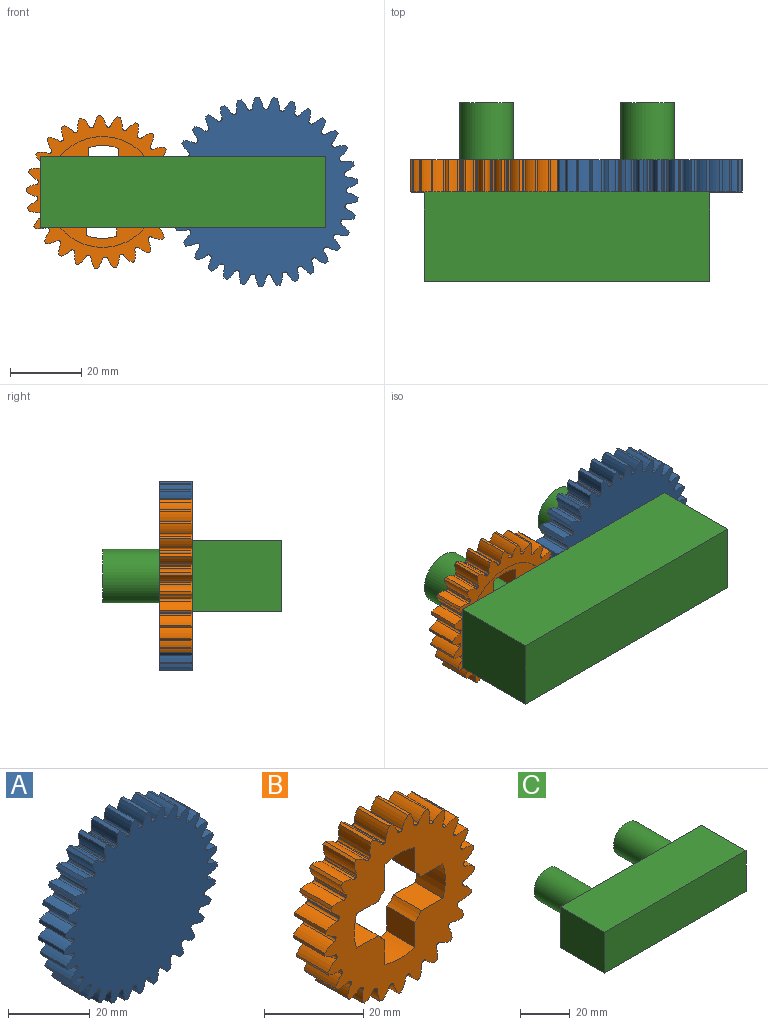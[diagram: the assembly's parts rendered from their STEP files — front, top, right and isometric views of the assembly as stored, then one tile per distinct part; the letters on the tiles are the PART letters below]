
ASSEMBLY  parts=3 mates=2
PART A: 200 faces, bbox 53x9x52.9 mm
  f0: cylinder r=26.51mm len=9mm, axis (0,1,0), area 10mm2, adj f32,f34,f190,f197
  f1: cylinder r=26.51mm len=9mm, axis (0,1,0), area 10mm2, adj f32,f34,f185,f192
  f2: cylinder r=26.51mm len=9mm, axis (0,1,0), area 10mm2, adj f32,f34,f180,f187
  f3: cylinder r=26.51mm len=9mm, axis (0,1,0), area 10mm2, adj f32,f34,f170,f182
  f4: cylinder r=26.51mm len=9mm, axis (0,1,0), area 10mm2, adj f32,f34,f165,f177
  f5: cylinder r=26.51mm len=9mm, axis (0,1,0), area 10mm2, adj f32,f34,f172,f175
  f6: cylinder r=26.51mm len=9mm, axis (0,1,0), area 10mm2, adj f32,f34,f160,f167
  f7: cylinder r=26.51mm len=9mm, axis (0,1,0), area 10mm2, adj f32,f34,f35,f162
  f8: cylinder r=26.51mm len=9mm, axis (0,1,0), area 10mm2, adj f32,f34,f150,f157
  f9: cylinder r=26.51mm len=9mm, axis (0,1,0), area 10mm2, adj f32,f34,f145,f152
  f10: cylinder r=26.51mm len=9mm, axis (0,1,0), area 10mm2, adj f32,f34,f140,f147
  f11: cylinder r=26.51mm len=9mm, axis (0,1,0), area 10mm2, adj f32,f34,f130,f142
  f12: cylinder r=26.51mm len=9mm, axis (0,1,0), area 10mm2, adj f32,f34,f125,f137
  f13: cylinder r=26.51mm len=9mm, axis (0,1,0), area 10mm2, adj f32,f34,f132,f135
  f14: cylinder r=26.51mm len=9mm, axis (0,1,0), area 10mm2, adj f32,f34,f120,f127
  f15: cylinder r=26.51mm len=9mm, axis (0,1,0), area 10mm2, adj f32,f34,f122,f195
  f16: cylinder r=26.51mm len=9mm, axis (0,1,0), area 10mm2, adj f32,f34,f110,f117
  f17: cylinder r=26.51mm len=9mm, axis (0,1,0), area 10mm2, adj f32,f34,f100,f112
  f18: cylinder r=26.51mm len=9mm, axis (0,1,0), area 10mm2, adj f32,f34,f95,f107
  f19: cylinder r=26.51mm len=9mm, axis (0,1,0), area 10mm2, adj f32,f34,f102,f105
  f20: cylinder r=26.51mm len=9mm, axis (0,1,0), area 10mm2, adj f32,f34,f90,f97
  f21: cylinder r=26.51mm len=9mm, axis (0,1,0), area 10mm2, adj f32,f34,f85,f92
  f22: cylinder r=26.51mm len=9mm, axis (0,1,0), area 10mm2, adj f32,f34,f80,f87
  f23: cylinder r=26.51mm len=9mm, axis (0,1,0), area 10mm2, adj f32,f34,f82,f155
  f24: cylinder r=26.51mm len=9mm, axis (0,1,0), area 10mm2, adj f32,f34,f70,f77
  f25: cylinder r=26.51mm len=9mm, axis (0,1,0), area 10mm2, adj f32,f34,f60,f72
  f26: cylinder r=26.51mm len=9mm, axis (0,1,0), area 10mm2, adj f32,f34,f55,f67
  f27: cylinder r=26.51mm len=9mm, axis (0,1,0), area 10mm2, adj f32,f34,f62,f65
  f28: cylinder r=26.51mm len=9mm, axis (0,1,0), area 10mm2, adj f32,f34,f50,f57
  f29: cylinder r=26.51mm len=9mm, axis (0,1,0), area 10mm2, adj f32,f34,f45,f52
  f30: cylinder r=26.51mm len=9mm, axis (0,1,0), area 10mm2, adj f32,f34,f40,f47
  f31: cylinder r=26.51mm len=9mm, axis (0,1,0), area 10mm2, adj f32,f34,f42,f115
  f32: plane 53x52.95mm, normal (0,1,0), area 1956.6mm2, adj f0,f1,f2,f3,f4,f5,f6,f7
  f33: cylinder r=26.51mm len=9mm, axis (0,1,0), area 10mm2, adj f32,f34,f37,f75
  f34: plane 53x52.95mm, normal (0,-1,0), area 1956.6mm2, adj f0,f1,f2,f3,f4,f5,f6,f7
  f35: cylinder r=8.46mm len=9mm, axis (0,1,0), area 27.8mm2, adj f7,f32,f34,f38
  f36: cylinder r=23.2mm len=9mm, axis (0,1,0), area 2.8mm2, adj f32,f34,f38,f39
  f37: cylinder r=8.46mm len=9mm, axis (0,1,0), area 27.8mm2, adj f32,f33,f34,f39
  f38: cylinder r=0.57mm len=9mm, axis (0,1,0), area 6.9mm2, adj f32,f34,f35,f36
  f39: cylinder r=0.57mm len=9mm, axis (0,1,0), area 6.9mm2, adj f32,f34,f36,f37
  f40: cylinder r=8.46mm len=9mm, axis (0,1,0), area 27.8mm2, adj f30,f32,f34,f43
  f41: cylinder r=23.2mm len=9mm, axis (0,1,0), area 2.8mm2, adj f32,f34,f43,f44
  f42: cylinder r=8.46mm len=9mm, axis (0,1,0), area 27.8mm2, adj f31,f32,f34,f44
  f43: cylinder r=0.57mm len=9mm, axis (0,1,0), area 6.9mm2, adj f32,f34,f40,f41
  f44: cylinder r=0.57mm len=9mm, axis (0,1,0), area 6.9mm2, adj f32,f34,f41,f42
  f45: cylinder r=8.46mm len=9mm, axis (0,1,0), area 27.8mm2, adj f29,f32,f34,f48
  f46: cylinder r=23.2mm len=9mm, axis (0,1,0), area 2.8mm2, adj f32,f34,f48,f49
  f47: cylinder r=8.46mm len=9mm, axis (0,1,0), area 27.8mm2, adj f30,f32,f34,f49
  f48: cylinder r=0.57mm len=9mm, axis (0,1,0), area 6.9mm2, adj f32,f34,f45,f46
  f49: cylinder r=0.57mm len=9mm, axis (0,1,0), area 6.9mm2, adj f32,f34,f46,f47
  f50: cylinder r=8.46mm len=9mm, axis (0,1,0), area 27.8mm2, adj f28,f32,f34,f53
  f51: cylinder r=23.2mm len=9mm, axis (0,1,0), area 2.8mm2, adj f32,f34,f53,f54
  f52: cylinder r=8.46mm len=9mm, axis (0,1,0), area 27.8mm2, adj f29,f32,f34,f54
  f53: cylinder r=0.57mm len=9mm, axis (0,1,0), area 6.9mm2, adj f32,f34,f50,f51
  f54: cylinder r=0.57mm len=9mm, axis (0,1,0), area 6.9mm2, adj f32,f34,f51,f52
  f55: cylinder r=8.46mm len=9mm, axis (0,1,0), area 27.8mm2, adj f26,f32,f34,f58
  f56: cylinder r=23.2mm len=9mm, axis (0,1,0), area 2.8mm2, adj f32,f34,f58,f59
  f57: cylinder r=8.46mm len=9mm, axis (0,1,0), area 27.8mm2, adj f28,f32,f34,f59
  f58: cylinder r=0.57mm len=9mm, axis (0,1,0), area 6.9mm2, adj f32,f34,f55,f56
  f59: cylinder r=0.57mm len=9mm, axis (0,1,0), area 6.9mm2, adj f32,f34,f56,f57
  f60: cylinder r=8.46mm len=9mm, axis (0,1,0), area 27.8mm2, adj f25,f32,f34,f63
  f61: cylinder r=23.2mm len=9mm, axis (0,1,0), area 2.8mm2, adj f32,f34,f63,f64
  f62: cylinder r=8.46mm len=9mm, axis (0,1,0), area 27.8mm2, adj f27,f32,f34,f64
  f63: cylinder r=0.57mm len=9mm, axis (0,1,0), area 6.9mm2, adj f32,f34,f60,f61
  f64: cylinder r=0.57mm len=9mm, axis (0,1,0), area 6.9mm2, adj f32,f34,f61,f62
  f65: cylinder r=8.46mm len=9mm, axis (0,1,0), area 27.8mm2, adj f27,f32,f34,f68
  f66: cylinder r=23.2mm len=9mm, axis (0,1,0), area 2.8mm2, adj f32,f34,f68,f69
  f67: cylinder r=8.46mm len=9mm, axis (0,1,0), area 27.8mm2, adj f26,f32,f34,f69
  f68: cylinder r=0.57mm len=9mm, axis (0,1,0), area 6.9mm2, adj f32,f34,f65,f66
  f69: cylinder r=0.57mm len=9mm, axis (0,1,0), area 6.9mm2, adj f32,f34,f66,f67
  f70: cylinder r=8.46mm len=9mm, axis (0,1,0), area 27.8mm2, adj f24,f32,f34,f73
  f71: cylinder r=23.2mm len=9mm, axis (0,1,0), area 2.8mm2, adj f32,f34,f73,f74
  f72: cylinder r=8.46mm len=9mm, axis (0,1,0), area 27.8mm2, adj f25,f32,f34,f74
  f73: cylinder r=0.57mm len=9mm, axis (0,1,0), area 6.9mm2, adj f32,f34,f70,f71
  f74: cylinder r=0.57mm len=9mm, axis (0,1,0), area 6.9mm2, adj f32,f34,f71,f72
  f75: cylinder r=8.46mm len=9mm, axis (0,1,0), area 27.8mm2, adj f32,f33,f34,f78
  f76: cylinder r=23.2mm len=9mm, axis (0,1,0), area 2.8mm2, adj f32,f34,f78,f79
  f77: cylinder r=8.46mm len=9mm, axis (0,1,0), area 27.8mm2, adj f24,f32,f34,f79
  f78: cylinder r=0.57mm len=9mm, axis (0,1,0), area 6.9mm2, adj f32,f34,f75,f76
  f79: cylinder r=0.57mm len=9mm, axis (0,1,0), area 6.9mm2, adj f32,f34,f76,f77
  f80: cylinder r=8.46mm len=9mm, axis (0,1,0), area 27.8mm2, adj f22,f32,f34,f83
  f81: cylinder r=23.2mm len=9mm, axis (0,1,0), area 2.8mm2, adj f32,f34,f83,f84
  f82: cylinder r=8.46mm len=9mm, axis (0,1,0), area 27.8mm2, adj f23,f32,f34,f84
  f83: cylinder r=0.57mm len=9mm, axis (0,1,0), area 6.9mm2, adj f32,f34,f80,f81
  f84: cylinder r=0.57mm len=9mm, axis (0,1,0), area 6.9mm2, adj f32,f34,f81,f82
  f85: cylinder r=8.46mm len=9mm, axis (0,1,0), area 27.8mm2, adj f21,f32,f34,f88
  f86: cylinder r=23.2mm len=9mm, axis (0,1,0), area 2.8mm2, adj f32,f34,f88,f89
  f87: cylinder r=8.46mm len=9mm, axis (0,1,0), area 27.8mm2, adj f22,f32,f34,f89
  f88: cylinder r=0.57mm len=9mm, axis (0,1,0), area 6.9mm2, adj f32,f34,f85,f86
  f89: cylinder r=0.57mm len=9mm, axis (0,1,0), area 6.9mm2, adj f32,f34,f86,f87
  f90: cylinder r=8.46mm len=9mm, axis (0,1,0), area 27.8mm2, adj f20,f32,f34,f93
  f91: cylinder r=23.2mm len=9mm, axis (0,1,0), area 2.8mm2, adj f32,f34,f93,f94
  f92: cylinder r=8.46mm len=9mm, axis (0,1,0), area 27.8mm2, adj f21,f32,f34,f94
  f93: cylinder r=0.57mm len=9mm, axis (0,1,0), area 6.9mm2, adj f32,f34,f90,f91
  f94: cylinder r=0.57mm len=9mm, axis (0,1,0), area 6.9mm2, adj f32,f34,f91,f92
  f95: cylinder r=8.46mm len=9mm, axis (0,1,0), area 27.8mm2, adj f18,f32,f34,f98
  f96: cylinder r=23.2mm len=9mm, axis (0,1,0), area 2.8mm2, adj f32,f34,f98,f99
  f97: cylinder r=8.46mm len=9mm, axis (0,1,0), area 27.8mm2, adj f20,f32,f34,f99
  f98: cylinder r=0.57mm len=9mm, axis (0,1,0), area 6.9mm2, adj f32,f34,f95,f96
  f99: cylinder r=0.57mm len=9mm, axis (0,1,0), area 6.9mm2, adj f32,f34,f96,f97
  f100: cylinder r=8.46mm len=9mm, axis (0,1,0), area 27.8mm2, adj f17,f32,f34,f103
  f101: cylinder r=23.2mm len=9mm, axis (0,1,0), area 2.8mm2, adj f32,f34,f103,f104
  f102: cylinder r=8.46mm len=9mm, axis (0,1,0), area 27.8mm2, adj f19,f32,f34,f104
  f103: cylinder r=0.57mm len=9mm, axis (0,1,0), area 6.9mm2, adj f32,f34,f100,f101
  f104: cylinder r=0.57mm len=9mm, axis (0,1,0), area 6.9mm2, adj f32,f34,f101,f102
  f105: cylinder r=8.46mm len=9mm, axis (0,1,0), area 27.8mm2, adj f19,f32,f34,f108
  f106: cylinder r=23.2mm len=9mm, axis (0,1,0), area 2.8mm2, adj f32,f34,f108,f109
  f107: cylinder r=8.46mm len=9mm, axis (0,1,0), area 27.8mm2, adj f18,f32,f34,f109
  f108: cylinder r=0.57mm len=9mm, axis (0,1,0), area 6.9mm2, adj f32,f34,f105,f106
  f109: cylinder r=0.57mm len=9mm, axis (0,1,0), area 6.9mm2, adj f32,f34,f106,f107
  f110: cylinder r=8.46mm len=9mm, axis (0,1,0), area 27.8mm2, adj f16,f32,f34,f113
  f111: cylinder r=23.2mm len=9mm, axis (0,1,0), area 2.8mm2, adj f32,f34,f113,f114
  f112: cylinder r=8.46mm len=9mm, axis (0,1,0), area 27.8mm2, adj f17,f32,f34,f114
  f113: cylinder r=0.57mm len=9mm, axis (0,1,0), area 6.9mm2, adj f32,f34,f110,f111
  f114: cylinder r=0.57mm len=9mm, axis (0,1,0), area 6.9mm2, adj f32,f34,f111,f112
  f115: cylinder r=8.46mm len=9mm, axis (0,1,0), area 27.8mm2, adj f31,f32,f34,f118
  f116: cylinder r=23.2mm len=9mm, axis (0,1,0), area 2.8mm2, adj f32,f34,f118,f119
  f117: cylinder r=8.46mm len=9mm, axis (0,1,0), area 27.8mm2, adj f16,f32,f34,f119
  f118: cylinder r=0.57mm len=9mm, axis (0,1,0), area 6.9mm2, adj f32,f34,f115,f116
  f119: cylinder r=0.57mm len=9mm, axis (0,1,0), area 6.9mm2, adj f32,f34,f116,f117
  f120: cylinder r=8.46mm len=9mm, axis (0,1,0), area 27.8mm2, adj f14,f32,f34,f123
  f121: cylinder r=23.2mm len=9mm, axis (0,1,0), area 2.8mm2, adj f32,f34,f123,f124
  f122: cylinder r=8.46mm len=9mm, axis (0,1,0), area 27.8mm2, adj f15,f32,f34,f124
  f123: cylinder r=0.57mm len=9mm, axis (0,1,0), area 6.9mm2, adj f32,f34,f120,f121
  f124: cylinder r=0.57mm len=9mm, axis (0,1,0), area 6.9mm2, adj f32,f34,f121,f122
  f125: cylinder r=8.46mm len=9mm, axis (0,1,0), area 27.8mm2, adj f12,f32,f34,f128
  f126: cylinder r=23.2mm len=9mm, axis (0,1,0), area 2.8mm2, adj f32,f34,f128,f129
  f127: cylinder r=8.46mm len=9mm, axis (0,1,0), area 27.8mm2, adj f14,f32,f34,f129
  f128: cylinder r=0.57mm len=9mm, axis (0,1,0), area 6.9mm2, adj f32,f34,f125,f126
  f129: cylinder r=0.57mm len=9mm, axis (0,1,0), area 6.9mm2, adj f32,f34,f126,f127
  f130: cylinder r=8.46mm len=9mm, axis (0,1,0), area 27.8mm2, adj f11,f32,f34,f133
  f131: cylinder r=23.2mm len=9mm, axis (0,1,0), area 2.8mm2, adj f32,f34,f133,f134
  f132: cylinder r=8.46mm len=9mm, axis (0,1,0), area 27.8mm2, adj f13,f32,f34,f134
  f133: cylinder r=0.57mm len=9mm, axis (0,1,0), area 6.9mm2, adj f32,f34,f130,f131
  f134: cylinder r=0.57mm len=9mm, axis (0,1,0), area 6.9mm2, adj f32,f34,f131,f132
  f135: cylinder r=8.46mm len=9mm, axis (0,1,0), area 27.8mm2, adj f13,f32,f34,f138
  f136: cylinder r=23.2mm len=9mm, axis (0,1,0), area 2.8mm2, adj f32,f34,f138,f139
  f137: cylinder r=8.46mm len=9mm, axis (0,1,0), area 27.8mm2, adj f12,f32,f34,f139
  f138: cylinder r=0.57mm len=9mm, axis (0,1,0), area 6.9mm2, adj f32,f34,f135,f136
  f139: cylinder r=0.57mm len=9mm, axis (0,1,0), area 6.9mm2, adj f32,f34,f136,f137
  f140: cylinder r=8.46mm len=9mm, axis (0,1,0), area 27.8mm2, adj f10,f32,f34,f143
  f141: cylinder r=23.2mm len=9mm, axis (0,1,0), area 2.8mm2, adj f32,f34,f143,f144
  f142: cylinder r=8.46mm len=9mm, axis (0,1,0), area 27.8mm2, adj f11,f32,f34,f144
  f143: cylinder r=0.57mm len=9mm, axis (0,1,0), area 6.9mm2, adj f32,f34,f140,f141
  f144: cylinder r=0.57mm len=9mm, axis (0,1,0), area 6.9mm2, adj f32,f34,f141,f142
  f145: cylinder r=8.46mm len=9mm, axis (0,1,0), area 27.8mm2, adj f9,f32,f34,f148
  f146: cylinder r=23.2mm len=9mm, axis (0,1,0), area 2.8mm2, adj f32,f34,f148,f149
  f147: cylinder r=8.46mm len=9mm, axis (0,1,0), area 27.8mm2, adj f10,f32,f34,f149
  f148: cylinder r=0.57mm len=9mm, axis (0,1,0), area 6.9mm2, adj f32,f34,f145,f146
  f149: cylinder r=0.57mm len=9mm, axis (0,1,0), area 6.9mm2, adj f32,f34,f146,f147
  f150: cylinder r=8.46mm len=9mm, axis (0,1,0), area 27.8mm2, adj f8,f32,f34,f153
  f151: cylinder r=23.2mm len=9mm, axis (0,1,0), area 2.8mm2, adj f32,f34,f153,f154
  f152: cylinder r=8.46mm len=9mm, axis (0,1,0), area 27.8mm2, adj f9,f32,f34,f154
  f153: cylinder r=0.57mm len=9mm, axis (0,1,0), area 6.9mm2, adj f32,f34,f150,f151
  f154: cylinder r=0.57mm len=9mm, axis (0,1,0), area 6.9mm2, adj f32,f34,f151,f152
  f155: cylinder r=8.46mm len=9mm, axis (0,1,0), area 27.8mm2, adj f23,f32,f34,f158
  f156: cylinder r=23.2mm len=9mm, axis (0,1,0), area 2.8mm2, adj f32,f34,f158,f159
  f157: cylinder r=8.46mm len=9mm, axis (0,1,0), area 27.8mm2, adj f8,f32,f34,f159
  f158: cylinder r=0.57mm len=9mm, axis (0,1,0), area 6.9mm2, adj f32,f34,f155,f156
  f159: cylinder r=0.57mm len=9mm, axis (0,1,0), area 6.9mm2, adj f32,f34,f156,f157
  f160: cylinder r=8.46mm len=9mm, axis (0,1,0), area 27.8mm2, adj f6,f32,f34,f163
  f161: cylinder r=23.2mm len=9mm, axis (0,1,0), area 2.8mm2, adj f32,f34,f163,f164
  f162: cylinder r=8.46mm len=9mm, axis (0,1,0), area 27.8mm2, adj f7,f32,f34,f164
  f163: cylinder r=0.57mm len=9mm, axis (0,1,0), area 6.9mm2, adj f32,f34,f160,f161
  f164: cylinder r=0.57mm len=9mm, axis (0,1,0), area 6.9mm2, adj f32,f34,f161,f162
  f165: cylinder r=8.46mm len=9mm, axis (0,1,0), area 27.8mm2, adj f4,f32,f34,f168
  f166: cylinder r=23.2mm len=9mm, axis (0,1,0), area 2.8mm2, adj f32,f34,f168,f169
  f167: cylinder r=8.46mm len=9mm, axis (0,1,0), area 27.8mm2, adj f6,f32,f34,f169
  f168: cylinder r=0.57mm len=9mm, axis (0,1,0), area 6.9mm2, adj f32,f34,f165,f166
  f169: cylinder r=0.57mm len=9mm, axis (0,1,0), area 6.9mm2, adj f32,f34,f166,f167
  f170: cylinder r=8.46mm len=9mm, axis (0,1,0), area 27.8mm2, adj f3,f32,f34,f173
  f171: cylinder r=23.2mm len=9mm, axis (0,1,0), area 2.8mm2, adj f32,f34,f173,f174
  f172: cylinder r=8.46mm len=9mm, axis (0,1,0), area 27.8mm2, adj f5,f32,f34,f174
  f173: cylinder r=0.57mm len=9mm, axis (0,1,0), area 6.9mm2, adj f32,f34,f170,f171
  f174: cylinder r=0.57mm len=9mm, axis (0,1,0), area 6.9mm2, adj f32,f34,f171,f172
  f175: cylinder r=8.46mm len=9mm, axis (0,1,0), area 27.8mm2, adj f5,f32,f34,f178
  f176: cylinder r=23.2mm len=9mm, axis (0,1,0), area 2.8mm2, adj f32,f34,f178,f179
  f177: cylinder r=8.46mm len=9mm, axis (0,1,0), area 27.8mm2, adj f4,f32,f34,f179
  f178: cylinder r=0.57mm len=9mm, axis (0,1,0), area 6.9mm2, adj f32,f34,f175,f176
  f179: cylinder r=0.57mm len=9mm, axis (0,1,0), area 6.9mm2, adj f32,f34,f176,f177
  f180: cylinder r=8.46mm len=9mm, axis (0,1,0), area 27.8mm2, adj f2,f32,f34,f183
  f181: cylinder r=23.2mm len=9mm, axis (0,1,0), area 2.8mm2, adj f32,f34,f183,f184
  f182: cylinder r=8.46mm len=9mm, axis (0,1,0), area 27.8mm2, adj f3,f32,f34,f184
  f183: cylinder r=0.57mm len=9mm, axis (0,1,0), area 6.9mm2, adj f32,f34,f180,f181
  f184: cylinder r=0.57mm len=9mm, axis (0,1,0), area 6.9mm2, adj f32,f34,f181,f182
  f185: cylinder r=8.46mm len=9mm, axis (0,1,0), area 27.8mm2, adj f1,f32,f34,f188
  f186: cylinder r=23.2mm len=9mm, axis (0,1,0), area 2.8mm2, adj f32,f34,f188,f189
  f187: cylinder r=8.46mm len=9mm, axis (0,1,0), area 27.8mm2, adj f2,f32,f34,f189
  f188: cylinder r=0.57mm len=9mm, axis (0,1,0), area 6.9mm2, adj f32,f34,f185,f186
  f189: cylinder r=0.57mm len=9mm, axis (0,1,0), area 6.9mm2, adj f32,f34,f186,f187
  f190: cylinder r=8.46mm len=9mm, axis (0,1,0), area 27.8mm2, adj f0,f32,f34,f193
  f191: cylinder r=23.2mm len=9mm, axis (0,1,0), area 2.8mm2, adj f32,f34,f193,f194
  f192: cylinder r=8.46mm len=9mm, axis (0,1,0), area 27.8mm2, adj f1,f32,f34,f194
  f193: cylinder r=0.57mm len=9mm, axis (0,1,0), area 6.9mm2, adj f32,f34,f190,f191
  f194: cylinder r=0.57mm len=9mm, axis (0,1,0), area 6.9mm2, adj f32,f34,f191,f192
  f195: cylinder r=8.46mm len=9mm, axis (0,1,0), area 27.8mm2, adj f15,f32,f34,f198
  f196: cylinder r=23.2mm len=9mm, axis (0,1,0), area 2.8mm2, adj f32,f34,f198,f199
  f197: cylinder r=8.46mm len=9mm, axis (0,1,0), area 27.8mm2, adj f0,f32,f34,f199
  f198: cylinder r=0.57mm len=9mm, axis (0,1,0), area 6.9mm2, adj f32,f34,f195,f196
  f199: cylinder r=0.57mm len=9mm, axis (0,1,0), area 6.9mm2, adj f32,f34,f196,f197
PART B: 170 faces, bbox 42.8x9x42.7 mm
  f0: plane 42.8x42.72mm, normal (0,1,0), area 489.9mm2, adj f6,f7,f8,f9,f10,f11,f12,f13
  f1: plane 42.8x42.72mm, normal (0,-1,0), area 874.6mm2, adj f2,f3,f4,f5,f6,f7,f8,f9
  f2: cylinder r=7.5mm len=7.9mm, axis (0,1,0), area 21.7mm2, adj f1,f164,f165,f169
  f3: cylinder r=7.5mm len=7.9mm, axis (0,1,0), area 21.7mm2, adj f1,f161,f162,f169
  f4: cylinder r=7.5mm len=7.9mm, axis (0,1,0), area 21.7mm2, adj f1,f158,f159,f169
  f5: cylinder r=7.5mm len=7.9mm, axis (0,1,0), area 21.7mm2, adj f1,f156,f167,f169
  f6: cylinder r=21.42mm len=9mm, axis (0,1,0), area 6.7mm2, adj f0,f1,f146,f153
  f7: cylinder r=21.42mm len=9mm, axis (0,1,0), area 6.7mm2, adj f0,f1,f131,f148
  f8: cylinder r=21.42mm len=9mm, axis (0,1,0), area 6.7mm2, adj f0,f1,f143,f151
  f9: cylinder r=21.42mm len=9mm, axis (0,1,0), area 6.7mm2, adj f0,f1,f138,f141
  f10: cylinder r=21.42mm len=9mm, axis (0,1,0), area 6.7mm2, adj f0,f1,f126,f133
  f11: cylinder r=21.42mm len=9mm, axis (0,1,0), area 6.7mm2, adj f0,f1,f121,f128
  f12: cylinder r=21.42mm len=9mm, axis (0,1,0), area 6.7mm2, adj f0,f1,f116,f123
  f13: cylinder r=21.42mm len=9mm, axis (0,1,0), area 6.7mm2, adj f0,f1,f106,f118
  f14: cylinder r=21.42mm len=9mm, axis (0,1,0), area 6.7mm2, adj f0,f1,f101,f113
  f15: cylinder r=21.42mm len=9mm, axis (0,1,0), area 6.7mm2, adj f0,f1,f108,f111
  f16: cylinder r=21.42mm len=9mm, axis (0,1,0), area 6.7mm2, adj f0,f1,f96,f103
  f17: cylinder r=21.42mm len=9mm, axis (0,1,0), area 6.7mm2, adj f0,f1,f91,f98
  f18: cylinder r=21.42mm len=9mm, axis (0,1,0), area 6.7mm2, adj f0,f1,f86,f93
  f19: cylinder r=21.42mm len=9mm, axis (0,1,0), area 6.7mm2, adj f0,f1,f76,f88
  f20: cylinder r=21.42mm len=9mm, axis (0,1,0), area 6.7mm2, adj f0,f1,f71,f83
  f21: cylinder r=21.42mm len=9mm, axis (0,1,0), area 6.7mm2, adj f0,f1,f78,f81
  f22: cylinder r=21.42mm len=9mm, axis (0,1,0), area 6.7mm2, adj f0,f1,f66,f73
  f23: cylinder r=21.42mm len=9mm, axis (0,1,0), area 6.7mm2, adj f0,f1,f61,f68
  f24: cylinder r=21.42mm len=9mm, axis (0,1,0), area 6.7mm2, adj f0,f1,f56,f63
  f25: cylinder r=21.42mm len=9mm, axis (0,1,0), area 6.7mm2, adj f0,f1,f41,f58
  f26: cylinder r=21.42mm len=9mm, axis (0,1,0), area 6.7mm2, adj f0,f1,f31,f53
  f27: cylinder r=21.42mm len=9mm, axis (0,1,0), area 6.7mm2, adj f0,f1,f48,f51
  f28: cylinder r=21.42mm len=9mm, axis (0,1,0), area 6.7mm2, adj f0,f1,f36,f43
  f29: cylinder r=21.42mm len=9mm, axis (0,1,0), area 6.7mm2, adj f0,f1,f38,f46
  f30: cylinder r=21.42mm len=9mm, axis (0,1,0), area 6.7mm2, adj f0,f1,f33,f136
  f31: cylinder r=6.41mm len=9mm, axis (0,1,0), area 28.7mm2, adj f0,f1,f26,f34
  f32: cylinder r=18.23mm len=9mm, axis (0,1,0), area 1.8mm2, adj f0,f1,f34,f35
  f33: cylinder r=6.41mm len=9mm, axis (0,1,0), area 28.7mm2, adj f0,f1,f30,f35
  f34: cylinder r=0.57mm len=9mm, axis (0,1,0), area 6.5mm2, adj f0,f1,f31,f32
  f35: cylinder r=0.57mm len=9mm, axis (0,1,0), area 6.5mm2, adj f0,f1,f32,f33
  f36: cylinder r=6.41mm len=9mm, axis (0,1,0), area 28.7mm2, adj f0,f1,f28,f39
  f37: cylinder r=18.23mm len=9mm, axis (0,1,0), area 1.8mm2, adj f0,f1,f39,f40
  f38: cylinder r=6.41mm len=9mm, axis (0,1,0), area 28.7mm2, adj f0,f1,f29,f40
  f39: cylinder r=0.57mm len=9mm, axis (0,1,0), area 6.5mm2, adj f0,f1,f36,f37
  f40: cylinder r=0.57mm len=9mm, axis (0,1,0), area 6.5mm2, adj f0,f1,f37,f38
  f41: cylinder r=6.41mm len=9mm, axis (0,1,0), area 28.7mm2, adj f0,f1,f25,f44
  f42: cylinder r=18.23mm len=9mm, axis (0,1,0), area 1.8mm2, adj f0,f1,f44,f45
  f43: cylinder r=6.41mm len=9mm, axis (0,1,0), area 28.7mm2, adj f0,f1,f28,f45
  f44: cylinder r=0.57mm len=9mm, axis (0,1,0), area 6.5mm2, adj f0,f1,f41,f42
  f45: cylinder r=0.57mm len=9mm, axis (0,1,0), area 6.5mm2, adj f0,f1,f42,f43
  f46: cylinder r=6.41mm len=9mm, axis (0,1,0), area 28.7mm2, adj f0,f1,f29,f49
  f47: cylinder r=18.23mm len=9mm, axis (0,1,0), area 1.8mm2, adj f0,f1,f49,f50
  f48: cylinder r=6.41mm len=9mm, axis (0,1,0), area 28.7mm2, adj f0,f1,f27,f50
  f49: cylinder r=0.57mm len=9mm, axis (0,1,0), area 6.5mm2, adj f0,f1,f46,f47
  f50: cylinder r=0.57mm len=9mm, axis (0,1,0), area 6.5mm2, adj f0,f1,f47,f48
  f51: cylinder r=6.41mm len=9mm, axis (0,1,0), area 28.7mm2, adj f0,f1,f27,f54
  f52: cylinder r=18.23mm len=9mm, axis (0,1,0), area 1.8mm2, adj f0,f1,f54,f55
  f53: cylinder r=6.41mm len=9mm, axis (0,1,0), area 28.7mm2, adj f0,f1,f26,f55
  f54: cylinder r=0.57mm len=9mm, axis (0,1,0), area 6.5mm2, adj f0,f1,f51,f52
  f55: cylinder r=0.57mm len=9mm, axis (0,1,0), area 6.5mm2, adj f0,f1,f52,f53
  f56: cylinder r=6.41mm len=9mm, axis (0,1,0), area 28.7mm2, adj f0,f1,f24,f59
  f57: cylinder r=18.23mm len=9mm, axis (0,1,0), area 1.8mm2, adj f0,f1,f59,f60
  f58: cylinder r=6.41mm len=9mm, axis (0,1,0), area 28.7mm2, adj f0,f1,f25,f60
  f59: cylinder r=0.57mm len=9mm, axis (0,1,0), area 6.5mm2, adj f0,f1,f56,f57
  f60: cylinder r=0.57mm len=9mm, axis (0,1,0), area 6.5mm2, adj f0,f1,f57,f58
  f61: cylinder r=6.41mm len=9mm, axis (0,1,0), area 28.7mm2, adj f0,f1,f23,f64
  f62: cylinder r=18.23mm len=9mm, axis (0,1,0), area 1.8mm2, adj f0,f1,f64,f65
  f63: cylinder r=6.41mm len=9mm, axis (0,1,0), area 28.7mm2, adj f0,f1,f24,f65
  f64: cylinder r=0.57mm len=9mm, axis (0,1,0), area 6.5mm2, adj f0,f1,f61,f62
  f65: cylinder r=0.57mm len=9mm, axis (0,1,0), area 6.5mm2, adj f0,f1,f62,f63
  f66: cylinder r=6.41mm len=9mm, axis (0,1,0), area 28.7mm2, adj f0,f1,f22,f69
  f67: cylinder r=18.23mm len=9mm, axis (0,1,0), area 1.8mm2, adj f0,f1,f69,f70
  f68: cylinder r=6.41mm len=9mm, axis (0,1,0), area 28.7mm2, adj f0,f1,f23,f70
  f69: cylinder r=0.57mm len=9mm, axis (0,1,0), area 6.5mm2, adj f0,f1,f66,f67
  f70: cylinder r=0.57mm len=9mm, axis (0,1,0), area 6.5mm2, adj f0,f1,f67,f68
  f71: cylinder r=6.41mm len=9mm, axis (0,1,0), area 28.7mm2, adj f0,f1,f20,f74
  f72: cylinder r=18.23mm len=9mm, axis (0,1,0), area 1.8mm2, adj f0,f1,f74,f75
  f73: cylinder r=6.41mm len=9mm, axis (0,1,0), area 28.7mm2, adj f0,f1,f22,f75
  f74: cylinder r=0.57mm len=9mm, axis (0,1,0), area 6.5mm2, adj f0,f1,f71,f72
  f75: cylinder r=0.57mm len=9mm, axis (0,1,0), area 6.5mm2, adj f0,f1,f72,f73
  f76: cylinder r=6.41mm len=9mm, axis (0,1,0), area 28.7mm2, adj f0,f1,f19,f79
  f77: cylinder r=18.23mm len=9mm, axis (0,1,0), area 1.8mm2, adj f0,f1,f79,f80
  f78: cylinder r=6.41mm len=9mm, axis (0,1,0), area 28.7mm2, adj f0,f1,f21,f80
  f79: cylinder r=0.57mm len=9mm, axis (0,1,0), area 6.5mm2, adj f0,f1,f76,f77
  f80: cylinder r=0.57mm len=9mm, axis (0,1,0), area 6.5mm2, adj f0,f1,f77,f78
  f81: cylinder r=6.41mm len=9mm, axis (0,1,0), area 28.7mm2, adj f0,f1,f21,f84
  f82: cylinder r=18.23mm len=9mm, axis (0,1,0), area 1.8mm2, adj f0,f1,f84,f85
  f83: cylinder r=6.41mm len=9mm, axis (0,1,0), area 28.7mm2, adj f0,f1,f20,f85
  f84: cylinder r=0.57mm len=9mm, axis (0,1,0), area 6.5mm2, adj f0,f1,f81,f82
  f85: cylinder r=0.57mm len=9mm, axis (0,1,0), area 6.5mm2, adj f0,f1,f82,f83
  f86: cylinder r=6.41mm len=9mm, axis (0,1,0), area 28.7mm2, adj f0,f1,f18,f89
  f87: cylinder r=18.23mm len=9mm, axis (0,1,0), area 1.8mm2, adj f0,f1,f89,f90
  f88: cylinder r=6.41mm len=9mm, axis (0,1,0), area 28.7mm2, adj f0,f1,f19,f90
  f89: cylinder r=0.57mm len=9mm, axis (0,1,0), area 6.5mm2, adj f0,f1,f86,f87
  f90: cylinder r=0.57mm len=9mm, axis (0,1,0), area 6.5mm2, adj f0,f1,f87,f88
  f91: cylinder r=6.41mm len=9mm, axis (0,1,0), area 28.7mm2, adj f0,f1,f17,f94
  f92: cylinder r=18.23mm len=9mm, axis (0,1,0), area 1.8mm2, adj f0,f1,f94,f95
  f93: cylinder r=6.41mm len=9mm, axis (0,1,0), area 28.7mm2, adj f0,f1,f18,f95
  f94: cylinder r=0.57mm len=9mm, axis (0,1,0), area 6.5mm2, adj f0,f1,f91,f92
  f95: cylinder r=0.57mm len=9mm, axis (0,1,0), area 6.5mm2, adj f0,f1,f92,f93
  f96: cylinder r=6.41mm len=9mm, axis (0,1,0), area 28.7mm2, adj f0,f1,f16,f99
  f97: cylinder r=18.23mm len=9mm, axis (0,1,0), area 1.8mm2, adj f0,f1,f99,f100
  f98: cylinder r=6.41mm len=9mm, axis (0,1,0), area 28.7mm2, adj f0,f1,f17,f100
  f99: cylinder r=0.57mm len=9mm, axis (0,1,0), area 6.5mm2, adj f0,f1,f96,f97
  f100: cylinder r=0.57mm len=9mm, axis (0,1,0), area 6.5mm2, adj f0,f1,f97,f98
  f101: cylinder r=6.41mm len=9mm, axis (0,1,0), area 28.7mm2, adj f0,f1,f14,f104
  f102: cylinder r=18.23mm len=9mm, axis (0,1,0), area 1.8mm2, adj f0,f1,f104,f105
  f103: cylinder r=6.41mm len=9mm, axis (0,1,0), area 28.7mm2, adj f0,f1,f16,f105
  f104: cylinder r=0.57mm len=9mm, axis (0,1,0), area 6.5mm2, adj f0,f1,f101,f102
  f105: cylinder r=0.57mm len=9mm, axis (0,1,0), area 6.5mm2, adj f0,f1,f102,f103
  f106: cylinder r=6.41mm len=9mm, axis (0,1,0), area 28.7mm2, adj f0,f1,f13,f109
  f107: cylinder r=18.23mm len=9mm, axis (0,1,0), area 1.8mm2, adj f0,f1,f109,f110
  f108: cylinder r=6.41mm len=9mm, axis (0,1,0), area 28.7mm2, adj f0,f1,f15,f110
  f109: cylinder r=0.57mm len=9mm, axis (0,1,0), area 6.5mm2, adj f0,f1,f106,f107
  f110: cylinder r=0.57mm len=9mm, axis (0,1,0), area 6.5mm2, adj f0,f1,f107,f108
  f111: cylinder r=6.41mm len=9mm, axis (0,1,0), area 28.7mm2, adj f0,f1,f15,f114
  f112: cylinder r=18.23mm len=9mm, axis (0,1,0), area 1.8mm2, adj f0,f1,f114,f115
  f113: cylinder r=6.41mm len=9mm, axis (0,1,0), area 28.7mm2, adj f0,f1,f14,f115
  f114: cylinder r=0.57mm len=9mm, axis (0,1,0), area 6.5mm2, adj f0,f1,f111,f112
  f115: cylinder r=0.57mm len=9mm, axis (0,1,0), area 6.5mm2, adj f0,f1,f112,f113
  f116: cylinder r=6.41mm len=9mm, axis (0,1,0), area 28.7mm2, adj f0,f1,f12,f119
  f117: cylinder r=18.23mm len=9mm, axis (0,1,0), area 1.8mm2, adj f0,f1,f119,f120
  f118: cylinder r=6.41mm len=9mm, axis (0,1,0), area 28.7mm2, adj f0,f1,f13,f120
  f119: cylinder r=0.57mm len=9mm, axis (0,1,0), area 6.5mm2, adj f0,f1,f116,f117
  f120: cylinder r=0.57mm len=9mm, axis (0,1,0), area 6.5mm2, adj f0,f1,f117,f118
  f121: cylinder r=6.41mm len=9mm, axis (0,1,0), area 28.7mm2, adj f0,f1,f11,f124
  f122: cylinder r=18.23mm len=9mm, axis (0,1,0), area 1.8mm2, adj f0,f1,f124,f125
  f123: cylinder r=6.41mm len=9mm, axis (0,1,0), area 28.7mm2, adj f0,f1,f12,f125
  f124: cylinder r=0.57mm len=9mm, axis (0,1,0), area 6.5mm2, adj f0,f1,f121,f122
  f125: cylinder r=0.57mm len=9mm, axis (0,1,0), area 6.5mm2, adj f0,f1,f122,f123
  f126: cylinder r=6.41mm len=9mm, axis (0,1,0), area 28.7mm2, adj f0,f1,f10,f129
  f127: cylinder r=18.23mm len=9mm, axis (0,1,0), area 1.8mm2, adj f0,f1,f129,f130
  f128: cylinder r=6.41mm len=9mm, axis (0,1,0), area 28.7mm2, adj f0,f1,f11,f130
  f129: cylinder r=0.57mm len=9mm, axis (0,1,0), area 6.5mm2, adj f0,f1,f126,f127
  f130: cylinder r=0.57mm len=9mm, axis (0,1,0), area 6.5mm2, adj f0,f1,f127,f128
  f131: cylinder r=6.41mm len=9mm, axis (0,1,0), area 28.7mm2, adj f0,f1,f7,f134
  f132: cylinder r=18.23mm len=9mm, axis (0,1,0), area 1.8mm2, adj f0,f1,f134,f135
  f133: cylinder r=6.41mm len=9mm, axis (0,1,0), area 28.7mm2, adj f0,f1,f10,f135
  f134: cylinder r=0.57mm len=9mm, axis (0,1,0), area 6.5mm2, adj f0,f1,f131,f132
  f135: cylinder r=0.57mm len=9mm, axis (0,1,0), area 6.5mm2, adj f0,f1,f132,f133
  f136: cylinder r=6.41mm len=9mm, axis (0,1,0), area 28.7mm2, adj f0,f1,f30,f139
  f137: cylinder r=18.23mm len=9mm, axis (0,1,0), area 1.8mm2, adj f0,f1,f139,f140
  f138: cylinder r=6.41mm len=9mm, axis (0,1,0), area 28.7mm2, adj f0,f1,f9,f140
  f139: cylinder r=0.57mm len=9mm, axis (0,1,0), area 6.5mm2, adj f0,f1,f136,f137
  f140: cylinder r=0.57mm len=9mm, axis (0,1,0), area 6.5mm2, adj f0,f1,f137,f138
  f141: cylinder r=6.41mm len=9mm, axis (0,1,0), area 28.7mm2, adj f0,f1,f9,f144
  f142: cylinder r=18.23mm len=9mm, axis (0,1,0), area 1.8mm2, adj f0,f1,f144,f145
  f143: cylinder r=6.41mm len=9mm, axis (0,1,0), area 28.7mm2, adj f0,f1,f8,f145
  f144: cylinder r=0.57mm len=9mm, axis (0,1,0), area 6.5mm2, adj f0,f1,f141,f142
  f145: cylinder r=0.57mm len=9mm, axis (0,1,0), area 6.5mm2, adj f0,f1,f142,f143
  f146: cylinder r=6.41mm len=9mm, axis (0,1,0), area 28.7mm2, adj f0,f1,f6,f149
  f147: cylinder r=18.23mm len=9mm, axis (0,1,0), area 1.8mm2, adj f0,f1,f149,f150
  f148: cylinder r=6.41mm len=9mm, axis (0,1,0), area 28.7mm2, adj f0,f1,f7,f150
  f149: cylinder r=0.57mm len=9mm, axis (0,1,0), area 6.5mm2, adj f0,f1,f146,f147
  f150: cylinder r=0.57mm len=9mm, axis (0,1,0), area 6.5mm2, adj f0,f1,f147,f148
  f151: cylinder r=6.41mm len=9mm, axis (0,1,0), area 28.7mm2, adj f0,f1,f8,f154
  f152: cylinder r=18.23mm len=9mm, axis (0,1,0), area 1.8mm2, adj f0,f1,f154,f155
  f153: cylinder r=6.41mm len=9mm, axis (0,1,0), area 28.7mm2, adj f0,f1,f6,f155
  f154: cylinder r=0.57mm len=9mm, axis (0,1,0), area 6.5mm2, adj f0,f1,f151,f152
  f155: cylinder r=0.57mm len=9mm, axis (0,1,0), area 6.5mm2, adj f0,f1,f152,f153
  f156: plane 7.9x6.11mm, normal (-1,0,0), area 48.2mm2, adj f1,f5,f157,f169
  f157: cylinder r=13mm len=8.5mm, axis (0,1,0), area 68.4mm2, adj f1,f156,f158,f169
  f158: plane 7.9x6.11mm, normal (1,0,0), area 48.2mm2, adj f1,f4,f157,f169
  f159: plane 7.9x6.11mm, normal (0,0,-1), area 48.2mm2, adj f1,f4,f160,f169
  f160: cylinder r=13mm len=8.5mm, axis (0,1,0), area 68.4mm2, adj f1,f159,f161,f169
  f161: plane 7.9x6.11mm, normal (0,0,1), area 48.2mm2, adj f1,f3,f160,f169
  f162: plane 7.9x6.11mm, normal (1,0,0), area 48.2mm2, adj f1,f3,f163,f169
  f163: cylinder r=13mm len=8.5mm, axis (0,1,0), area 68.4mm2, adj f1,f162,f164,f169
  f164: plane 7.9x6.11mm, normal (-1,0,0), area 48.2mm2, adj f1,f2,f163,f169
  f165: plane 7.9x6.11mm, normal (0,0,1), area 48.2mm2, adj f1,f2,f166,f169
  f166: cylinder r=13mm len=8.5mm, axis (0,1,0), area 68.4mm2, adj f1,f165,f167,f169
  f167: plane 7.9x6.11mm, normal (0,0,-1), area 48.2mm2, adj f1,f5,f166,f169
  f168: cylinder r=15.5mm len=31mm, axis (0,1,0), area 107.1mm2, adj f0,f169
  f169: plane 31x31mm, normal (0,1,0), area 384.7mm2, adj f2,f3,f4,f5,f156,f157,f158,f159
PART C: 10 faces, bbox 80x50x20 mm
  f0: plane 25x20mm, normal (1,0,0), area 500mm2, adj f1,f3,f4,f5
  f1: plane 80x25mm, normal (0,0,1), area 2000mm2, adj f0,f2,f4,f5
  f2: plane 25x20mm, normal (-1,0,0), area 500mm2, adj f1,f3,f4,f5
  f3: plane 80x25mm, normal (0,0,-1), area 2000mm2, adj f0,f2,f4,f5
  f4: plane 80x20mm, normal (0,-1,0), area 1600mm2, adj f0,f1,f2,f3
  f5: plane 80x20mm, normal (0,1,0), area 1246.6mm2, adj f0,f1,f2,f3,f6,f8
  f6: cylinder r=7.5mm len=25mm, axis (0,-1,0), area 1178.1mm2, adj f5,f7
  f7: plane 15x15mm, normal (0,1,0), area 176.7mm2, adj f6
  f8: cylinder r=7.5mm len=25mm, axis (0,-1,0), area 1178.1mm2, adj f5,f9
  f9: plane 15x15mm, normal (0,1,0), area 176.7mm2, adj f8
PLACE A rot(axis=(0,-1,0),31.1deg) t=(22.5,9,0)mm
PLACE B rot(axis=(-0.72,0,-0.7),180deg) t=(-22.5,0,0)mm
PLACE C at identity fixed
MATE revolute C.f6 <-> B.f168  axis (0,-1,0) through (-22.5,0,0)mm
MATE revolute A.f36 <-> C.f8  axis (0,-1,0) through (22.5,0,0)mm
